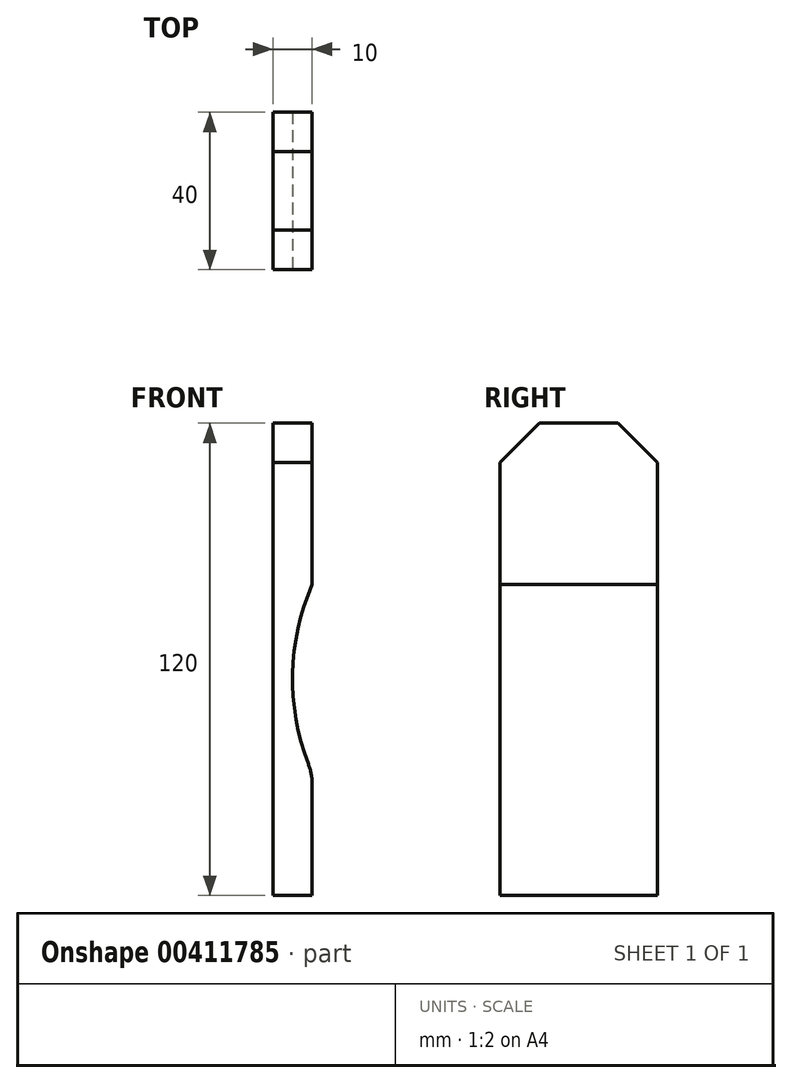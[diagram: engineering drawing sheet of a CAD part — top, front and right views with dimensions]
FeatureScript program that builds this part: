
annotation { "Feature Type Name" : "Feature", "Feature Type Description" : "" }
export const myFeature = defineFeature(function(context is Context, id is Id, definition is map)
    precondition{}
    {
        {
            var Q0;
            Q0=qCreatedBy(makeId("Front.planeOp"),FACE);
            var sketch = newSketch(context, id + "F0", { "sketchPlane" : qUnion([Q0])});
            skLineSegment(sketch, "E0.bottom", {"start": v(0, 0) * mm, "end": v(10, 0) * mm});
            skLineSegment(sketch, "E0.top", {"start": v(0, 120) * mm, "end": v(10, 120) * mm});
            skLineSegment(sketch, "E0.left", {"start": v(0, 0) * mm, "end": v(0, 120) * mm});
            skLineSegment(sketch, "E0.right", {"start": v(10, 0) * mm, "end": v(10, 120) * mm});
            skPoint(sketch, "E1.centerSnap0", {"position": v(10, 60) * mm});
            skSolve(sketch);
        }
        {
            var Q0;
            {var subQ1=sQuery(id+"F0.wireOp",EDGE,"E0.bottom");Q0=makeQuery(id+"F0.imprint","IMPRINT",FACE,{"disambiguationData":[TD([[makeQuery(id+"F0.imprint","IMPRINT",EDGE,{"derivedFrom":subQ1}),1.0]])]});}
            extrude(context, id + "F1", {"entities" : qUnion([Q0]), "oppositeDirection" : true, "depth" : 40 * mm});
        }
        {
            var Q0;
            Q0=makeQuery(id+"F1.opExtrude","CAP_EDGE",EDGE,{"disambiguationData":[OSD([sQuery(id+"F0.wireOp",EDGE,"E0.top")])],"isStart":true});
            var Q1;
            Q1=makeQuery(id+"F1.opExtrude","CAP_EDGE",EDGE,{"disambiguationData":[OSD([sQuery(id+"F0.wireOp",EDGE,"E0.top")])],"isStart":false});
            chamfer(context, id + "F2", {"entities" : qUnion([Q0, Q1]), "width" : 10 * mm, "tangentPropagation" : true});
        }
        {
            var Q0;
            Q0=makeQuery(id+"F1.opExtrude","CAP_FACE",FACE,{"disambiguationData":[OSD([sQuery(id+"F0.wireOp",EDGE,"E0.bottom"),sQuery(id+"F0.wireOp",EDGE,"E0.top"),sQuery(id+"F0.wireOp",EDGE,"E0.left"),sQuery(id+"F0.wireOp",EDGE,"E0.right")])],"isStart":true});
            var sketch = newSketch(context, id + "F3", { "sketchPlane" : qUnion([Q0])});
            skLineSegment(sketch, "E2.0", {"start": v(10, 0) * mm, "end": v(10, 110) * mm});
            skArc(sketch, "E3", {"start": v(10, 78.98) * mm, "mid": v(5, 55) * mm, "end": v(10, 31.02) * mm});
            skSolve(sketch);
        }
        {
            var Q0;
            Q0=qSketchRegion(id+"F3",true);
            var Q1;
            Q1=makeQuery(id+"F1.opExtrude","CAP_FACE",FACE,{"disambiguationData":[OSD([sQuery(id+"F0.wireOp",EDGE,"E0.bottom"),sQuery(id+"F0.wireOp",EDGE,"E0.top"),sQuery(id+"F0.wireOp",EDGE,"E0.left"),sQuery(id+"F0.wireOp",EDGE,"E0.right")])],"isStart":false});
            extrude(context, id + "F4", {"entities" : qUnion([Q0]), "operationType" : NewBodyOperationType.REMOVE, "endBound" : BoundingType.UP_TO_SURFACE, "oppositeDirection" : true, "endBoundEntityFace" : qUnion([Q1]), "depth" : 50.8 * mm});
        }
        {
            var Q0;
            {var subQ0=sQuery(id+"F3.wireOp",EDGE,"E3");var subQ1=sQuery(id+"F3.wireOp",EDGE,"E2.0");Q0=makeQuery(id+"F4.boolean.opBoolean","COPY",EDGE,{"derivedFrom":makeQuery(id+"F4.opExtrude","SWEPT_EDGE",EDGE,{"disambiguationData":[OSD([subQ1,subQ0]),TDD([makeQuery(id+"F3.imprint","INTERSECT",VERTEX,{"disambiguationData":[OD(0.0)],"derivedFrom":[subQ1,subQ0]})])]})});}
            var Q1;
            {var subQ0=sQuery(id+"F3.wireOp",EDGE,"E3");var subQ1=sQuery(id+"F3.wireOp",EDGE,"E2.0");Q1=makeQuery(id+"F4.boolean.opBoolean","COPY",EDGE,{"derivedFrom":makeQuery(id+"F4.opExtrude","SWEPT_EDGE",EDGE,{"disambiguationData":[OSD([subQ1,subQ0]),TDD([makeQuery(id+"F3.imprint","INTERSECT",VERTEX,{"disambiguationData":[OD(1.0)],"derivedFrom":[subQ1,subQ0]})])]})});}
            fillet(context, id + "F5", {"entities" : qUnion([Q0, Q1]), "radius" : 15 * mm, "tangentPropagation" : true, "allowEdgeOverflow" : false});
        }
    });
